# Revit family: Distanzbügel 300_FT_FS
name_source: partatom
category: Generic Models
revit_build: Autodesk Revit 2017 (Build: 20160225_1515(x64)
units: mm (PartAtom-declared; Revit-internal decimal feet)

## family parameters
Always vertical = Yes
Can host rebar = No
Cut with Voids When Loaded = No
Part Type = Normal
Room Calculation Point = No
Round Connector Dimension = Use Diameter
Shared = No
Work Plane-Based = No

## types (2) — shared parameters
Cut's number = 2
Length = 40 mm  [stored 0.131234 ft]
Manufacturer = OBO BETTERMANN
URL = http://www.obo-bettermann.com
Width = 300 mm
Width 1 = 150 mm  [stored 0.492126 ft]

## per-type parameters (varying)
| type | GTIN | Manufacturer Art.No. | Material |
| DBLG 20 300 FS | 4012196961702 | 6015670 | Strip-galvanised |
| DBLG 20 300 FT | 4012196043323 | 6015672 | Hot-dip galvanised |

note: column(s) folded — value = type name in every type: Article Type

note: [stored X ft] marks values corroborated as IEEE doubles in the binary element streams (Revit-internal decimal feet)

## geometry (parser evidence)
native form markers: Sweep x2
no freeform markers — native parametric forms only
